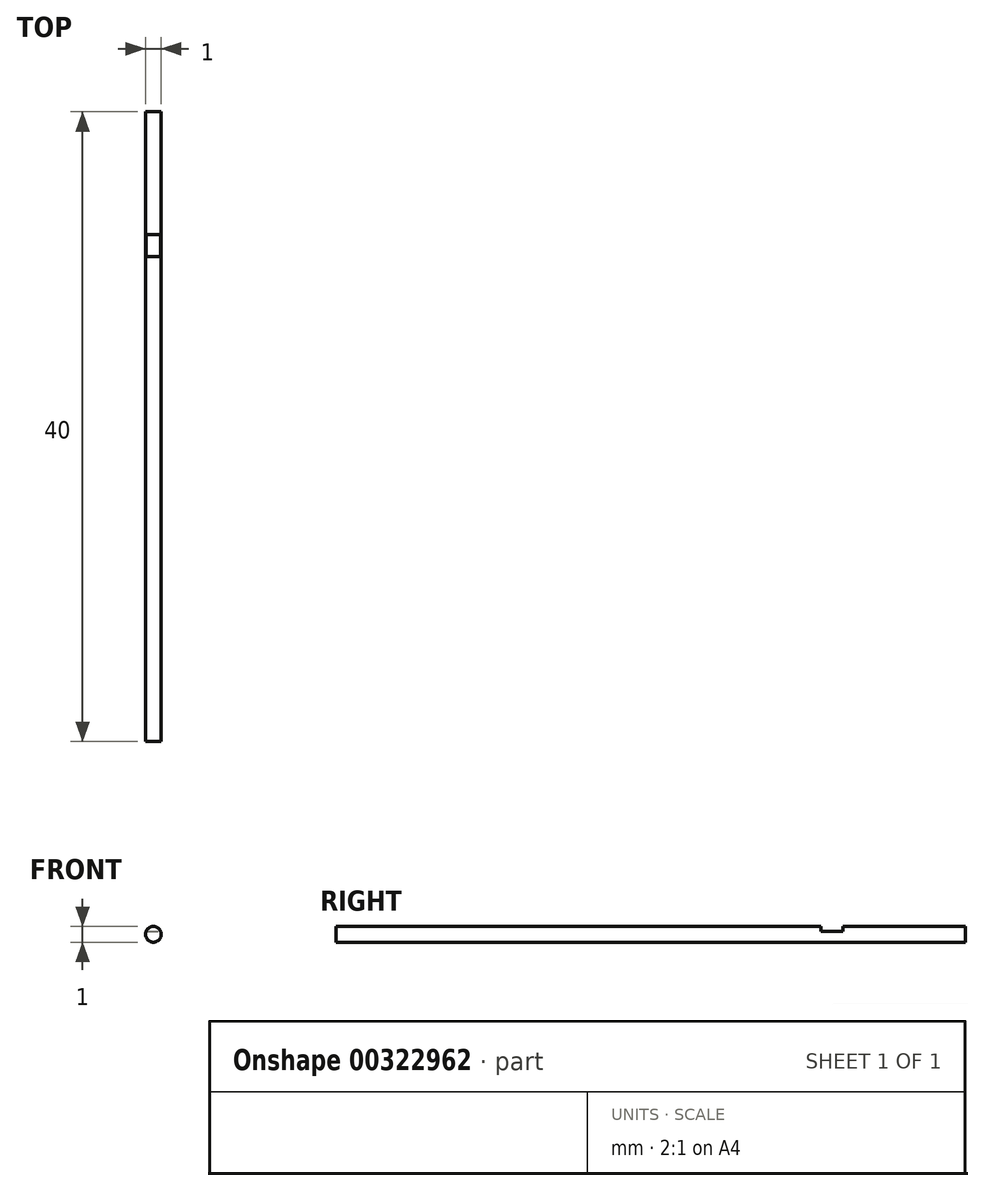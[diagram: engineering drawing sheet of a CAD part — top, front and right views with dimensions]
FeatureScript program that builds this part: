
annotation { "Feature Type Name" : "Feature", "Feature Type Description" : "" }
export const myFeature = defineFeature(function(context is Context, id is Id, definition is map)
    precondition{}
    {
        {
            var Q0;
            Q0=qCreatedBy(makeId("Front.planeOp"),FACE);
            var sketch = newSketch(context, id + "F0", { "sketchPlane" : qUnion([Q0])});
            skCircle(sketch, "E0", {"center": v(0, 0) * mm, "radius": 0.5 * mm});
            skSolve(sketch);
        }
        {
            var Q0;
            Q0=makeQuery(id+"F0.imprint","IMPRINT",FACE,{"disambiguationData":[TD([[makeQuery(id+"F0.imprint","IMPRINT",EDGE,{"derivedFrom":sQuery(id+"F0.wireOp",EDGE,"E0")}),1.0]])]});
            extrude(context, id + "F1", {"entities" : qUnion([Q0]), "depth" : 40 * mm});
        }
        {
            var Q0;
            Q0=qCreatedBy(makeId("Right.planeOp"),FACE);
            var sketch = newSketch(context, id + "F2", { "sketchPlane" : qUnion([Q0])});
            skLineSegment(sketch, "E1", {"start": v(0, 0) * mm, "end": v(-8.5, 0) * mm, "construction": true});
            skLineSegment(sketch, "E2", {"start": v(-8.5, 0) * mm, "end": v(-8.5, 0.5) * mm, "construction": true});
            skLineSegment(sketch, "E3.bottom", {"start": v(-7.8, 0.19) * mm, "end": v(-9.2, 0.19) * mm});
            skLineSegment(sketch, "E3.top", {"start": v(-7.8, 0.81) * mm, "end": v(-9.2, 0.81) * mm});
            skLineSegment(sketch, "E3.left", {"start": v(-7.8, 0.19) * mm, "end": v(-7.8, 0.81) * mm});
            skLineSegment(sketch, "E3.right", {"start": v(-9.2, 0.19) * mm, "end": v(-9.2, 0.81) * mm});
            skPoint(sketch, "E3.middle", {"position": v(-8.5, 0.5) * mm});
            skSolve(sketch);
        }
        {
            var Q0;
            Q0 = qSketchRegion(id + "F2", true);
            extrude(context, id + "F3", {"entities" : qUnion([Q0]), "operationType" : NewBodyOperationType.REMOVE, "oppositeDirection" : true, "depth" : 25 * mm, "symmetric" : true});
        }
    });
